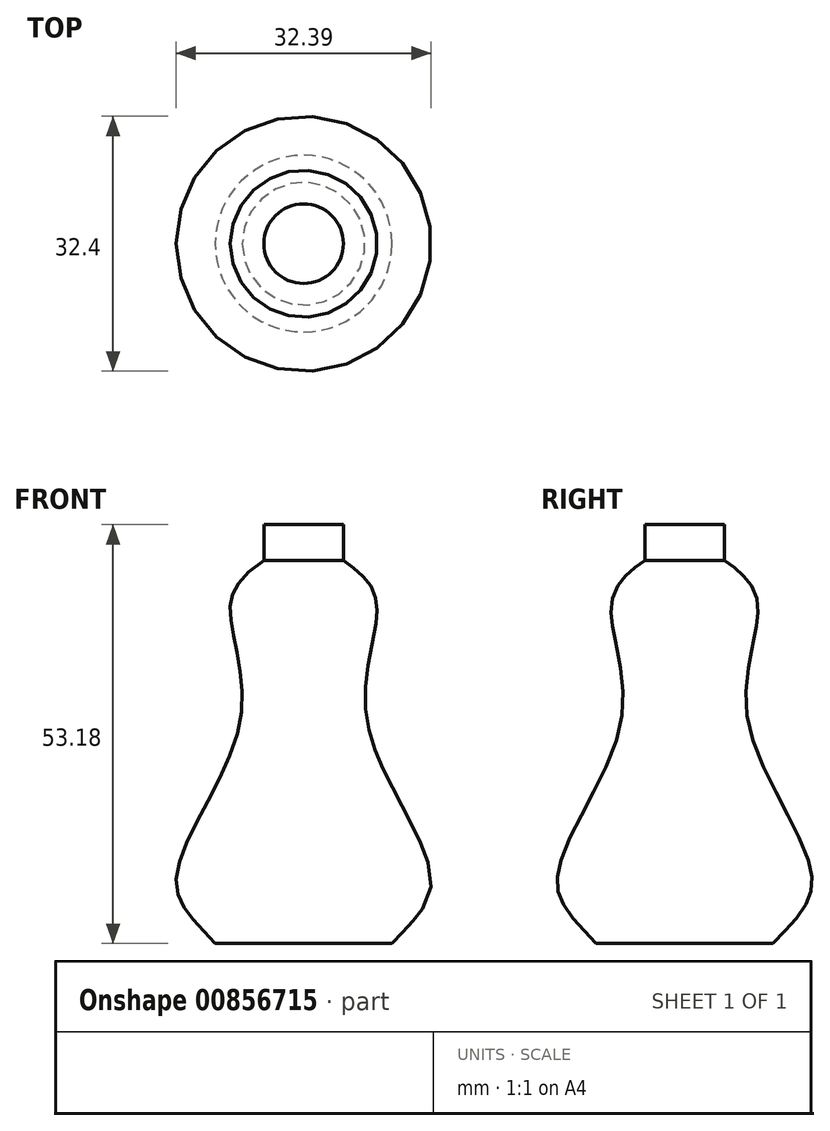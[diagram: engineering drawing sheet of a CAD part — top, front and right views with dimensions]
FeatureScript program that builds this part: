
annotation { "Feature Type Name" : "Feature", "Feature Type Description" : "" }
export const myFeature = defineFeature(function(context is Context, id is Id, definition is map)
    precondition{}
    {
        {
            var Q0;
            Q0=qCreatedBy(makeId("Front.planeOp"),FACE);
            var sketch = newSketch(context, id + "F0", { "sketchPlane" : qUnion([Q0])});
            skLineSegment(sketch, "E0", {"start": v(0, 0) * mm, "end": v(0, 53.18) * mm});
            skLineSegment(sketch, "E1", {"start": v(0, 53.18) * mm, "end": v(5.05, 53.18) * mm});
            skLineSegment(sketch, "E2", {"start": v(5.05, 53.18) * mm, "end": v(5.05, 48.64) * mm});
            skFitSpline(sketch, "E3", {"points": [v(5.05, 48.64) * mm, v(9.32, 41.84) * mm, v(8.15, 27.65) * mm, v(16.2, 8.04) * mm, v(11.23, 0) * mm], "startDerivative": vector(52.5, -35.55) * mm, "endDerivative": vector(-32.7, -36.17) * mm});
            skLineSegment(sketch, "E4", {"start": v(0, 0) * mm, "end": v(11.23, 0) * mm});
            skSolve(sketch);
        }
        {
            var Q0;
            Q0=makeQuery(id+"F0.imprint","IMPRINT",FACE,{"disambiguationData":[TD([[makeQuery(id+"F0.imprint","IMPRINT",EDGE,{"derivedFrom":sQuery(id+"F0.wireOp",EDGE,"E0")}),-1.0]])]});
            var Q1;
            Q1=sQuery(id+"F0.wireOp",EDGE,"E0");
            revolve(context, id + "F1", {"surfaceOperationType" : NewSurfaceOperationType.NEW, "entities" : qUnion([Q0]), "axis" : qUnion([Q1]), "revolveType" : RevolveType.FULL});
        }
    });
